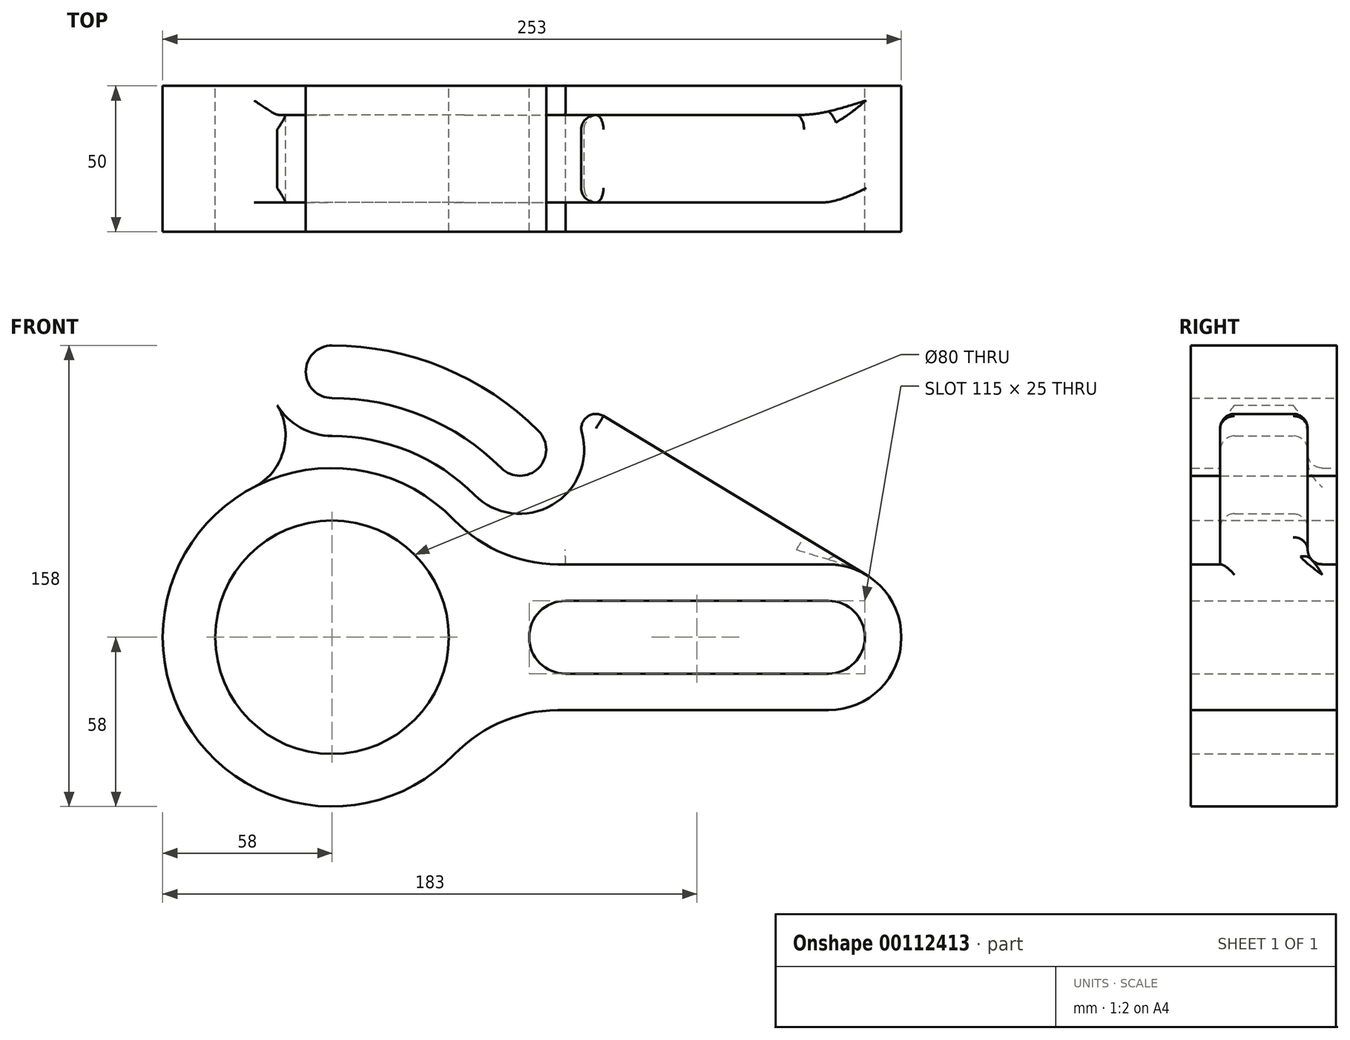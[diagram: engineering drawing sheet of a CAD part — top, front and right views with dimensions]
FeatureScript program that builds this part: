
annotation { "Feature Type Name" : "Feature", "Feature Type Description" : "" }
export const myFeature = defineFeature(function(context is Context, id is Id, definition is map)
    precondition{}
    {
        {
            var Q0;
            Q0=qCreatedBy(makeId("Front.planeOp"),FACE);
            var sketch = newSketch(context, id + "F0", { "sketchPlane" : qUnion([Q0])});
            skCircle(sketch, "E0", {"center": v(0, 0) * mm, "radius": 40 * mm});
            skLineSegment(sketch, "E1", {"start": v(80, 0) * mm, "end": v(170, 0) * mm, "construction": true});
            skArc(sketch, "E2.0.startCap", {"start": v(80, -12.5) * mm, "mid": v(67.5, 0) * mm, "end": v(80, 12.5) * mm});
            skArc(sketch, "E2.0.endCap", {"start": v(170, 12.5) * mm, "mid": v(182.5, 0) * mm, "end": v(170, -12.5) * mm});
            skLineSegment(sketch, "E2.0.left", {"start": v(80, 12.5) * mm, "end": v(170, 12.5) * mm});
            skLineSegment(sketch, "E2.0.right", {"start": v(80, -12.5) * mm, "end": v(170, -12.5) * mm});
            skArc(sketch, "E3", {"start": v(41.76, 40.25) * mm, "mid": v(-58, 0) * mm, "end": v(41.76, -40.25) * mm});
            skArc(sketch, "E4", {"start": v(170, 25) * mm, "mid": v(195, 0) * mm, "end": v(170, -25) * mm});
            skLineSegment(sketch, "E5", {"start": v(170, 25) * mm, "end": v(80, 25) * mm});
            skLineSegment(sketch, "E6", {"start": v(170, -25) * mm, "end": v(80, -25) * mm});
            skArc(sketch, "E7", {"start": v(41.76, 40.25) * mm, "mid": v(59.24, 28.5) * mm, "end": v(80, 25) * mm});
            skArc(sketch, "E8", {"start": v(41.76, -40.25) * mm, "mid": v(59.24, -28.5) * mm, "end": v(80, -25) * mm});
            skArc(sketch, "E9", {"start": v(0, 91) * mm, "mid": v(34.82, 84.07) * mm, "end": v(64.35, 64.35) * mm, "construction": true});
            skArc(sketch, "E10.0.startCap", {"start": v(0, 82) * mm, "mid": v(-9, 91) * mm, "end": v(0, 100) * mm});
            skArc(sketch, "E10.0.endCap", {"start": v(70.71, 70.71) * mm, "mid": v(70.71, 57.98) * mm, "end": v(57.98, 57.98) * mm});
            skArc(sketch, "E10.0.left", {"start": v(0, 100) * mm, "mid": v(38.27, 92.39) * mm, "end": v(70.71, 70.71) * mm});
            skArc(sketch, "E10.0.right", {"start": v(0, 82) * mm, "mid": v(31.38, 75.76) * mm, "end": v(57.98, 57.98) * mm});
            skArc(sketch, "E11.0", {"start": v(0, 113) * mm, "mid": v(43.24, 104.4) * mm, "end": v(79.9, 79.9) * mm});
            skArc(sketch, "E11.1", {"start": v(0, 69) * mm, "mid": v(-22, 91) * mm, "end": v(0, 113) * mm});
            skArc(sketch, "E11.2", {"start": v(0, 69) * mm, "mid": v(26.4, 63.75) * mm, "end": v(48.8, 48.8) * mm});
            skArc(sketch, "E11.3", {"start": v(79.9, 79.9) * mm, "mid": v(79.9, 48.8) * mm, "end": v(48.8, 48.8) * mm});
            skLineSegment(sketch, "E12", {"start": v(0, 0) * mm, "end": v(0, 23.21) * mm, "construction": true});
            skLineSegment(sketch, "E13", {"start": v(0, 23.21) * mm, "end": v(0, 0) * mm, "construction": true});
            skLineSegment(sketch, "E14", {"start": v(0, 0) * mm, "end": v(21.62, 21.62) * mm, "construction": true});
            skArc(sketch, "E15", {"start": v(-26.71, 51.48) * mm, "mid": v(-16.67, 63.83) * mm, "end": v(-18.82, 79.6) * mm});
            skLineSegment(sketch, "E16", {"start": v(182.94, 21.39) * mm, "end": v(58.5, 96.68) * mm});
            skSolve(sketch);
        }
        {
            var Q0;
            Q0=makeQuery(id+"F0.imprint","IMPRINT",FACE,{"disambiguationData":[TD([[makeQuery(id+"F0.imprint","IMPRINT",EDGE,{"derivedFrom":sQuery(id+"F0.wireOp",EDGE,"E0")}),-1.0]])]});
            extrude(context, id + "F1", {"entities" : qUnion([Q0]), "endBound" : BoundingType.SYMMETRIC, "depth" : 50 * mm});
        }
        {
            var Q0;
            Q0=makeQuery(id+"F0.imprint","IMPRINT",FACE,{"disambiguationData":[TD([[makeQuery(id+"F0.imprint","IMPRINT",EDGE,{"derivedFrom":sQuery(id+"F0.wireOp",EDGE,"E10.0.startCap")}),1.0]])]});
            extrude(context, id + "F2", {"entities" : qUnion([Q0]), "endBound" : BoundingType.SYMMETRIC, "depth" : 50 * mm});
        }
        {
            var Q0;
            {var subQ1=sQuery(id+"F0.wireOp",EDGE,"E5");Q0=makeQuery(id+"F0.imprint","IMPRINT",FACE,{"disambiguationData":[TD([[makeQuery(id+"F0.imprint","IMPRINT",EDGE,{"derivedFrom":subQ1}),-1.0]])]});}
            extrude(context, id + "F3", {"entities" : qUnion([Q0]), "operationType" : NewBodyOperationType.ADD, "endBound" : BoundingType.SYMMETRIC, "depth" : 30 * mm});
        }
        {
            var Q0;
            Q0=makeQuery(id+"F3.opExtrude","CAP_EDGE",EDGE,{"disambiguationData":[OSD([sQuery(id+"F0.wireOp",EDGE,"E7")])],"isStart":false});
            var Q1;
            Q1=makeQuery(id+"F3.opExtrude","CAP_EDGE",EDGE,{"disambiguationData":[OSD([sQuery(id+"F0.wireOp",EDGE,"E7")])],"isStart":true});
            fillet(context, id + "F4", {"entities" : qUnion([Q0, Q1]), "radius" : 5 * mm, "tangentPropagation" : true, "allowEdgeOverflow" : false});
        }
        {
            var Q0;
            Q0=makeQuery(id+"F3.opExtrude","CAP_EDGE",EDGE,{"disambiguationData":[OSD([sQuery(id+"F0.wireOp",EDGE,"E16")])],"isStart":true});
            var Q1;
            Q1=makeQuery(id+"F3.opExtrude","CAP_EDGE",EDGE,{"disambiguationData":[OSD([sQuery(id+"F0.wireOp",EDGE,"E16")])],"isStart":false});
            fillet(context, id + "F5", {"entities" : qUnion([Q0, Q1]), "radius" : 5 * mm, "tangentPropagation" : true, "allowEdgeOverflow" : false});
        }
        {
            var Q0;
            Q0=makeQuery(id+"F3.opExtrude","CAP_EDGE",EDGE,{"disambiguationData":[OSD([sQuery(id+"F0.wireOp",EDGE,"E11.3")])],"isStart":false});
            var Q1;
            Q1=makeQuery(id+"F3.opExtrude","CAP_EDGE",EDGE,{"disambiguationData":[OSD([sQuery(id+"F0.wireOp",EDGE,"E11.3")])],"isStart":true});
            fillet(context, id + "F6", {"entities" : qUnion([Q0, Q1]), "radius" : 5 * mm, "tangentPropagation" : true, "allowEdgeOverflow" : false});
        }
    });
